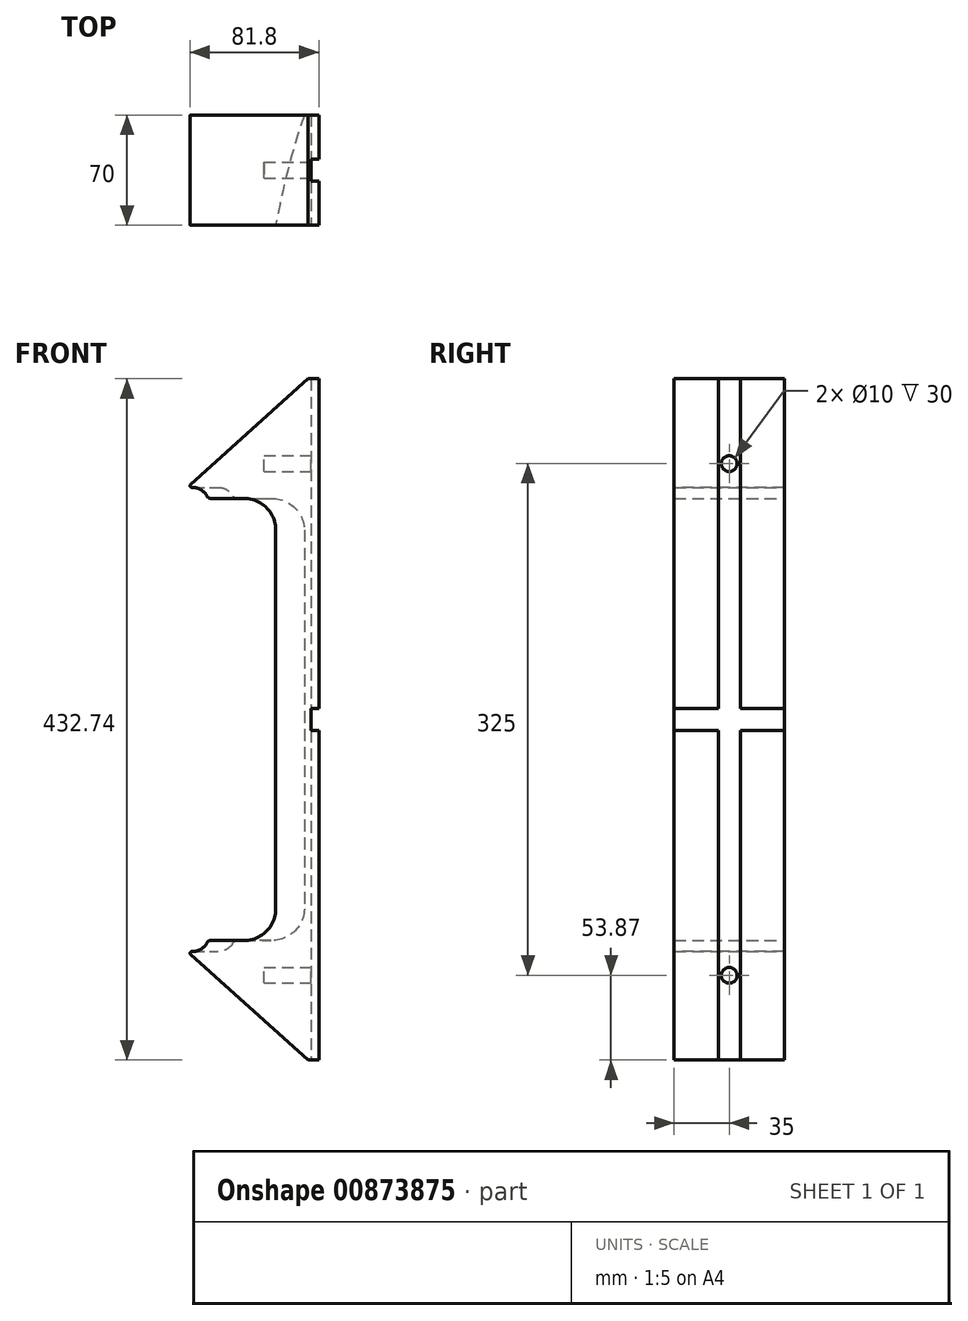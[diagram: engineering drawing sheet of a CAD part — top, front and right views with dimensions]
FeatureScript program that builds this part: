
annotation { "Feature Type Name" : "Feature", "Feature Type Description" : "" }
export const myFeature = defineFeature(function(context is Context, id is Id, definition is map)
    precondition{}
    {
        {
            var Q0;
            Q0=qCreatedBy(makeId("Front.planeOp"),FACE);
            var sketch = newSketch(context, id + "F0", { "sketchPlane" : qUnion([Q0])});
            skLineSegment(sketch, "E0", {"start": v(-480, 0) * mm, "end": v(-480, 120.4) * mm});
            skLineSegment(sketch, "E1", {"start": v(-500, 140.4) * mm, "end": v(-520.78, 140.4) * mm});
            skPoint(sketch, "E2.visualSharp", {"position": v(-480, 140.4) * mm});
            skArc(sketch, "E2.filletArc", {"start": v(-480, 120.4) * mm, "mid": v(-485.86, 134.54) * mm, "end": v(-500, 140.4) * mm});
            skArc(sketch, "E3", {"start": v(-523.02, 141.8) * mm, "mid": v(-526.7, 145.89) * mm, "end": v(-532, 147.4) * mm});
            skLineSegment(sketch, "E4", {"start": v(-450.85, 147.4) * mm, "end": v(-532, 147.4) * mm});
            skPoint(sketch, "E5.visualSharp", {"position": v(-522.46, 140.4) * mm});
            skArc(sketch, "E5.filletArc", {"start": v(-523.02, 141.8) * mm, "mid": v(-522.1, 140.78) * mm, "end": v(-520.78, 140.4) * mm});
            skLineSegment(sketch, "E6", {"start": v(-450.85, 147.4) * mm, "end": v(-450.85, 0) * mm});
            skArc(sketch, "E7.MirrorCS", {"start": v(-523.02, -141.8) * mm, "mid": v(-522.1, -140.78) * mm, "end": v(-520.78, -140.4) * mm});
            skArc(sketch, "E8.MirrorCS", {"start": v(-523.02, -141.8) * mm, "mid": v(-526.7, -145.89) * mm, "end": v(-532, -147.4) * mm});
            skArc(sketch, "E9.MirrorCS", {"start": v(-480, -120.4) * mm, "mid": v(-485.86, -134.54) * mm, "end": v(-500, -140.4) * mm});
            skLineSegment(sketch, "E10.MirrorCS", {"start": v(-450.85, -147.4) * mm, "end": v(-450.85, 0) * mm});
            skLineSegment(sketch, "E11.MirrorCS", {"start": v(-500, -140.4) * mm, "end": v(-520.78, -140.4) * mm});
            skLineSegment(sketch, "E12.MirrorCS", {"start": v(-450.85, -147.4) * mm, "end": v(-532, -147.4) * mm});
            skPoint(sketch, "E13.MirrorP", {"position": v(-480, -140.4) * mm});
            skLineSegment(sketch, "E14.MirrorCS", {"start": v(-480, 0) * mm, "end": v(-480, -120.4) * mm});
            skPoint(sketch, "E15.MirrorP", {"position": v(-522.46, -140.4) * mm});
            skSolve(sketch);
        }
        {
            var Q0;
            Q0=qCreatedBy(makeId("Top.planeOp"),FACE);
            var sketch = newSketch(context, id + "F1", { "sketchPlane" : qUnion([Q0])});
            skArc(sketch, "E16", {"start": v(-415.7, 240) * mm, "mid": v(-463.64, 124.23) * mm, "end": v(-480, 0) * mm});
            skLineSegment(sketch, "E17", {"start": v(0, 0) * mm, "end": v(-415.7, 240) * mm, "construction": true});
            skLineSegment(sketch, "E18", {"start": v(0, 0) * mm, "end": v(-480, 0) * mm, "construction": true});
            skSolve(sketch);
        }
        {
            var Q0;
            Q0=makeQuery(id+"F0.imprint","IMPRINT",FACE,{"disambiguationData":[TD([[makeQuery(id+"F0.imprint","IMPRINT",EDGE,{"derivedFrom":sQuery(id+"F0.wireOp",EDGE,"E0")}),-1.0]])]});
            var Q1;
            Q1=sQuery(id+"F1.wireOp",EDGE,"E16");
            sweep(context, id + "F2", {"profiles" : qUnion([Q0]), "path" : qUnion([Q1])});
        }
        {
            var Q0;
            Q0=makeQuery(id+"F2.opSweep","SWEPT_FACE",FACE,{"disambiguationData":[OSD([sQuery(id+"F0.wireOp",EDGE,"E4"),sQuery(id+"F1.wireOp",EDGE,"E16")])]});
            var sketch = newSketch(context, id + "F3", { "sketchPlane" : qUnion([Q0])});
            skLineSegment(sketch, "E19.bottom", {"start": v(-525.17, 85) * mm, "end": v(-445, 85) * mm});
            skLineSegment(sketch, "E20", {"start": v(0, 0) * mm, "end": v(-500, 0) * mm, "construction": true});
            skCircle(sketch, "E21", {"center": v(0, 0) * mm, "radius": 500 * mm, "construction": true});
            skLineSegment(sketch, "E22", {"start": v(-500, 0) * mm, "end": v(-500, 322.7) * mm, "construction": true});
            skLineSegment(sketch, "E23", {"start": v(-445, 85) * mm, "end": v(-445, 155) * mm});
            skLineSegment(sketch, "E24", {"start": v(-445, 155) * mm, "end": v(-508.92, 155) * mm});
            skArc(sketch, "E25", {"start": v(-390.45, 225.42) * mm, "mid": v(-435.49, 116.69) * mm, "end": v(-450.85, 0) * mm});
            skArc(sketch, "E26", {"start": v(-460.73, 266) * mm, "mid": v(-487.99, 211.87) * mm, "end": v(-508.92, 155) * mm});
            skLineSegment(sketch, "E27", {"start": v(-460.73, 266) * mm, "end": v(-390.45, 225.42) * mm});
            skLineSegment(sketch, "E28", {"start": v(-532, 0) * mm, "end": v(-450.85, 0) * mm});
            skArc(sketch, "E29.trimOffspring", {"start": v(-525.17, 85) * mm, "mid": v(-530.29, 42.64) * mm, "end": v(-532, 0) * mm});
            skPoint(sketch, "E30.start.orphan", {"position": v(-538.15, 155) * mm});
            skPoint(sketch, "E31.orphan", {"position": v(-538.15, 85) * mm});
            skSolve(sketch);
        }
        {
            var Q0;
            Q0=makeQuery(id+"F3.imprint","IMPRINT",FACE,{"disambiguationData":[TD([[makeQuery(id+"F3.imprint","IMPRINT",EDGE,{"derivedFrom":sQuery(id+"F3.wireOp",EDGE,"E19.bottom")}),-1.0]])]});
            var Q1;
            Q1=makeQuery(id+"F2.opSweep","SWEPT_FACE",FACE,{"disambiguationData":[OSD([sQuery(id+"F0.wireOp",EDGE,"E12.MirrorCS"),sQuery(id+"F1.wireOp",EDGE,"E16")])]});
            extrude(context, id + "F4", {"entities" : qUnion([Q0]), "operationType" : NewBodyOperationType.REMOVE, "endBound" : BoundingType.UP_TO_SURFACE, "oppositeDirection" : true, "depth" : 25 * mm, "endBoundEntityFace" : qUnion([Q1]), "offsetDistance" : 25 * mm});
        }
        {
            var Q0;
            Q0=makeQuery(id+"F4.boolean.opBoolean","COPY",FACE,{"derivedFrom":makeQuery(id+"F4.opExtrude","SWEPT_FACE",FACE,{"disambiguationData":[OSD([sQuery(id+"F3.wireOp",EDGE,"E19.bottom")])]})});
            var sketch = newSketch(context, id + "F5", { "sketchPlane" : qUnion([Q0])});
            skLineSegment(sketch, "E32", {"start": v(-445, 147.4) * mm, "end": v(-445, 222.5) * mm, "construction": true});
            skLineSegment(sketch, "E33", {"start": v(-445, 222.5) * mm, "end": v(-528.4, 147.4) * mm, "construction": true});
            skLineSegment(sketch, "E34", {"start": v(-528.4, 147.4) * mm, "end": v(-445, 147.4) * mm});
            skLineSegment(sketch, "E35", {"start": v(-451.8, 216.37) * mm, "end": v(-445, 216.37) * mm});
            skLineSegment(sketch, "E36", {"start": v(-445, 216.37) * mm, "end": v(-445, 147.4) * mm});
            skLineSegment(sketch, "E37", {"start": v(-528.4, 147.4) * mm, "end": v(-451.8, 216.37) * mm});
            skLineSegment(sketch, "E38.MirrorCS", {"start": v(-451.8, -216.37) * mm, "end": v(-445, -216.37) * mm});
            skLineSegment(sketch, "E39.MirrorCS", {"start": v(-528.4, -147.4) * mm, "end": v(-451.8, -216.37) * mm});
            skLineSegment(sketch, "E40.MirrorCS", {"start": v(-445, -216.37) * mm, "end": v(-445, -147.4) * mm});
            skLineSegment(sketch, "E41.MirrorCS", {"start": v(-445, -147.4) * mm, "end": v(-445, -222.5) * mm, "construction": true});
            skLineSegment(sketch, "E42.MirrorCS", {"start": v(-528.4, -147.4) * mm, "end": v(-445, -147.4) * mm});
            skLineSegment(sketch, "E43.MirrorCS", {"start": v(-445, -222.5) * mm, "end": v(-528.4, -147.4) * mm, "construction": true});
            skSolve(sketch);
        }
        {
            var Q0;
            Q0 = qSketchRegion(id + "F5", true);
            extrude(context, id + "F6", {"entities" : qUnion([Q0]), "operationType" : NewBodyOperationType.ADD, "oppositeDirection" : true, "depth" : 70 * mm, "offsetDistance" : 25 * mm});
        }
        {
            var Q0;
            Q0=makeQuery(id+"F6.boolean.opBoolean","MERGE",FACE,{"derivedFrom":[makeQuery(id+"F4.boolean.opBoolean","COPY",FACE,{"derivedFrom":makeQuery(id+"F4.opExtrude","SWEPT_FACE",FACE,{"disambiguationData":[OSD([sQuery(id+"F3.wireOp",EDGE,"E23")])]})}),makeQuery(id+"F6.opExtrude","SWEPT_FACE",FACE,{"disambiguationData":[OSD([sQuery(id+"F5.wireOp",EDGE,"E36")])]}),makeQuery(id+"F6.opExtrude","SWEPT_FACE",FACE,{"disambiguationData":[OSD([sQuery(id+"F5.wireOp",EDGE,"E40.MirrorCS")])]})]});
            var sketch = newSketch(context, id + "F7", { "sketchPlane" : qUnion([Q0])});
            skLineSegment(sketch, "E44.bottom", {"start": v(113, 216.37) * mm, "end": v(127, 216.37) * mm});
            skLineSegment(sketch, "E44.top", {"start": v(113, -216.37) * mm, "end": v(127, -216.37) * mm});
            skLineSegment(sketch, "E44.left", {"start": v(113, 216.37) * mm, "end": v(113, 7) * mm});
            skLineSegment(sketch, "E44.right", {"start": v(127, 216.37) * mm, "end": v(127, 7) * mm});
            skLineSegment(sketch, "E45.bottom", {"start": v(155, -7) * mm, "end": v(127, -7) * mm});
            skLineSegment(sketch, "E45.top", {"start": v(155, 7) * mm, "end": v(127, 7) * mm});
            skLineSegment(sketch, "E45.left", {"start": v(155, -7) * mm, "end": v(155, 7) * mm});
            skLineSegment(sketch, "E45.right", {"start": v(85, -7) * mm, "end": v(85, 7) * mm});
            skLineSegment(sketch, "E46.trimOffspring", {"start": v(113, 7) * mm, "end": v(85, 7) * mm});
            skLineSegment(sketch, "E47.trimOffspring", {"start": v(127, -7) * mm, "end": v(127, -216.37) * mm});
            skLineSegment(sketch, "E48.trimOffspring", {"start": v(113, -7) * mm, "end": v(85, -7) * mm});
            skLineSegment(sketch, "E49.trimOffspring", {"start": v(113, -7) * mm, "end": v(113, -216.37) * mm});
            skSolve(sketch);
        }
        {
            var Q0;
            Q0 = qSketchRegion(id + "F7", true);
            extrude(context, id + "F8", {"entities" : qUnion([Q0]), "operationType" : NewBodyOperationType.REMOVE, "oppositeDirection" : true, "depth" : 5 * mm, "offsetDistance" : 25 * mm});
        }
        {
            var Q0;
            Q0=makeQuery(id+"F8.boolean.opBoolean","COPY",FACE,{"derivedFrom":makeQuery(id+"F8.opExtrude","CAP_FACE",FACE,{"disambiguationData":[OSD([sQuery(id+"F7.wireOp",EDGE,"E44.bottom"),sQuery(id+"F7.wireOp",EDGE,"E44.top"),sQuery(id+"F7.wireOp",EDGE,"E44.left"),sQuery(id+"F7.wireOp",EDGE,"E44.right"),sQuery(id+"F7.wireOp",EDGE,"E45.bottom"),sQuery(id+"F7.wireOp",EDGE,"E45.top"),sQuery(id+"F7.wireOp",EDGE,"E45.left"),sQuery(id+"F7.wireOp",EDGE,"E45.right"),sQuery(id+"F7.wireOp",EDGE,"E46.trimOffspring"),sQuery(id+"F7.wireOp",EDGE,"E47.trimOffspring"),sQuery(id+"F7.wireOp",EDGE,"E48.trimOffspring"),sQuery(id+"F7.wireOp",EDGE,"E49.trimOffspring")])],"isStart":false})});
            var sketch = newSketch(context, id + "F9", { "sketchPlane" : qUnion([Q0])});
            skCircle(sketch, "E50", {"center": v(120, 162.5) * mm, "radius": 5 * mm});
            skCircle(sketch, "E51", {"center": v(120, -162.5) * mm, "radius": 5 * mm});
            skSolve(sketch);
        }
        {
            var Q0;
            Q0 = qSketchRegion(id + "F9", true);
            extrude(context, id + "F10", {"entities" : qUnion([Q0]), "operationType" : NewBodyOperationType.REMOVE, "oppositeDirection" : true, "depth" : 30 * mm, "offsetDistance" : 25 * mm});
        }
        {
            var Q0;
            Q0=makeQuery(id+"F6.opExtrude","SWEPT_EDGE",EDGE,{"disambiguationData":[OSD([sQuery(id+"F5.wireOp",EDGE,"E34"),sQuery(id+"F5.wireOp",EDGE,"E37")])]});
            var Q1;
            Q1=makeQuery(id+"F6.opExtrude","SWEPT_EDGE",EDGE,{"disambiguationData":[OSD([sQuery(id+"F5.wireOp",EDGE,"E39.MirrorCS"),sQuery(id+"F5.wireOp",EDGE,"E42.MirrorCS")])]});
            fillet(context, id + "F11", {"entities" : qUnion([Q0, Q1]), "radius" : 1 * mm, "tangentPropagation" : true, "allowEdgeOverflow" : false});
        }
    });
